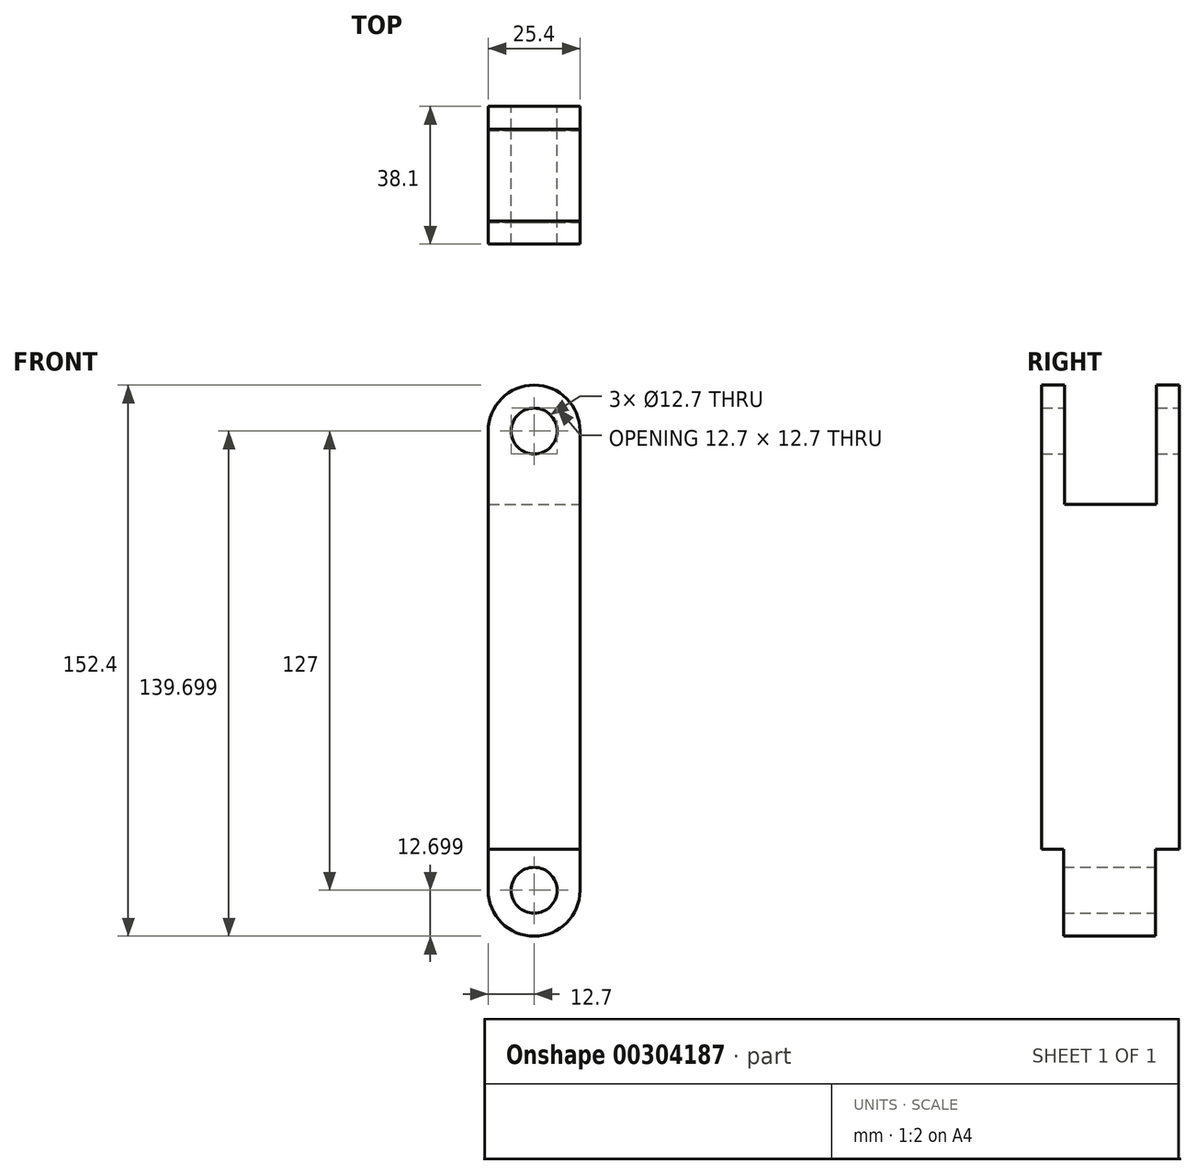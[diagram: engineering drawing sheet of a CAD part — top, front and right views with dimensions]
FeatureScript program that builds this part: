
annotation { "Feature Type Name" : "Feature", "Feature Type Description" : "" }
export const myFeature = defineFeature(function(context is Context, id is Id, definition is map)
    precondition{}
    {
        {
            var Q0;
            Q0=qCreatedBy(makeId("Front.planeOp"),FACE);
            var sketch = newSketch(context, id + "F0", { "sketchPlane" : qUnion([Q0])});
            skCircle(sketch, "E0", {"center": v(0, 104.4) * mm, "radius": 12.7 * mm});
            skCircle(sketch, "E1", {"center": v(0, 104.4) * mm, "radius": 6.35 * mm});
            skCircle(sketch, "E2", {"center": v(0, -22.6) * mm, "radius": 12.7 * mm});
            skCircle(sketch, "E3", {"center": v(0, -22.6) * mm, "radius": 6.35 * mm});
            skLineSegment(sketch, "E4", {"start": v(-12.7, 104.4) * mm, "end": v(-12.7, -22.6) * mm});
            skLineSegment(sketch, "E5", {"start": v(12.7, 104.4) * mm, "end": v(12.7, -22.6) * mm});
            skLineSegment(sketch, "E6", {"start": v(12.7, -22.6) * mm, "end": v(12.81, -24.02) * mm});
            skSolve(sketch);
        }
        {
            var Q0;
            Q0 = qSketchRegion(id + "F0", true);
            extrude(context, id + "F1", {"entities" : qUnion([Q0]), "endBound" : BoundingType.SYMMETRIC, "depth" : 38.1 * mm});
        }
        {
            var Q0;
            Q0=qCreatedBy(makeId("Right.planeOp"),FACE);
            var sketch = newSketch(context, id + "F2", { "sketchPlane" : qUnion([Q0])});
            skLineSegment(sketch, "E7.bottom", {"start": v(12.7, 84.19) * mm, "end": v(-12.7, 84.19) * mm});
            skLineSegment(sketch, "E7.top", {"start": v(12.7, 122.29) * mm, "end": v(-12.7, 122.29) * mm});
            skLineSegment(sketch, "E7.left", {"start": v(12.7, 84.19) * mm, "end": v(12.7, 122.29) * mm});
            skLineSegment(sketch, "E7.right", {"start": v(-12.7, 84.19) * mm, "end": v(-12.7, 122.29) * mm});
            skPoint(sketch, "E7.middle", {"position": v(0, 103.24) * mm});
            skSolve(sketch);
        }
        {
            var Q0;
            Q0 = qSketchRegion(id + "F2", true);
            extrude(context, id + "F3", {"entities" : qUnion([Q0]), "operationType" : NewBodyOperationType.REMOVE, "endBound" : BoundingType.SYMMETRIC, "oppositeDirection" : true, "depth" : 25.4 * mm});
        }
        {
            var Q0;
            Q0=qCreatedBy(makeId("Right.planeOp"),FACE);
            var sketch = newSketch(context, id + "F4", { "sketchPlane" : qUnion([Q0])});
            skLineSegment(sketch, "E8.bottom", {"start": v(-13.03, -36.58) * mm, "end": v(-20.65, -36.58) * mm});
            skLineSegment(sketch, "E8.top", {"start": v(-13.03, -11.18) * mm, "end": v(-20.65, -11.18) * mm});
            skLineSegment(sketch, "E8.left", {"start": v(-13.03, -36.58) * mm, "end": v(-13.03, -11.18) * mm});
            skLineSegment(sketch, "E8.right", {"start": v(-20.65, -36.58) * mm, "end": v(-20.65, -11.18) * mm});
            skPoint(sketch, "E8.middle", {"position": v(-16.84, -23.88) * mm});
            skLineSegment(sketch, "E9.bottom", {"start": v(20, -36.58) * mm, "end": v(12.37, -36.58) * mm});
            skLineSegment(sketch, "E9.top", {"start": v(20, -11.18) * mm, "end": v(12.37, -11.18) * mm});
            skLineSegment(sketch, "E9.left", {"start": v(20, -36.58) * mm, "end": v(20, -11.18) * mm});
            skLineSegment(sketch, "E9.right", {"start": v(12.37, -36.58) * mm, "end": v(12.37, -11.18) * mm});
            skPoint(sketch, "E9.middle", {"position": v(16.18, -23.88) * mm});
            skSolve(sketch);
        }
        {
            var Q0;
            Q0 = qSketchRegion(id + "F4", true);
            extrude(context, id + "F5", {"entities" : qUnion([Q0]), "operationType" : NewBodyOperationType.REMOVE, "endBound" : BoundingType.SYMMETRIC, "oppositeDirection" : true, "depth" : 25.4 * mm});
        }
    });
